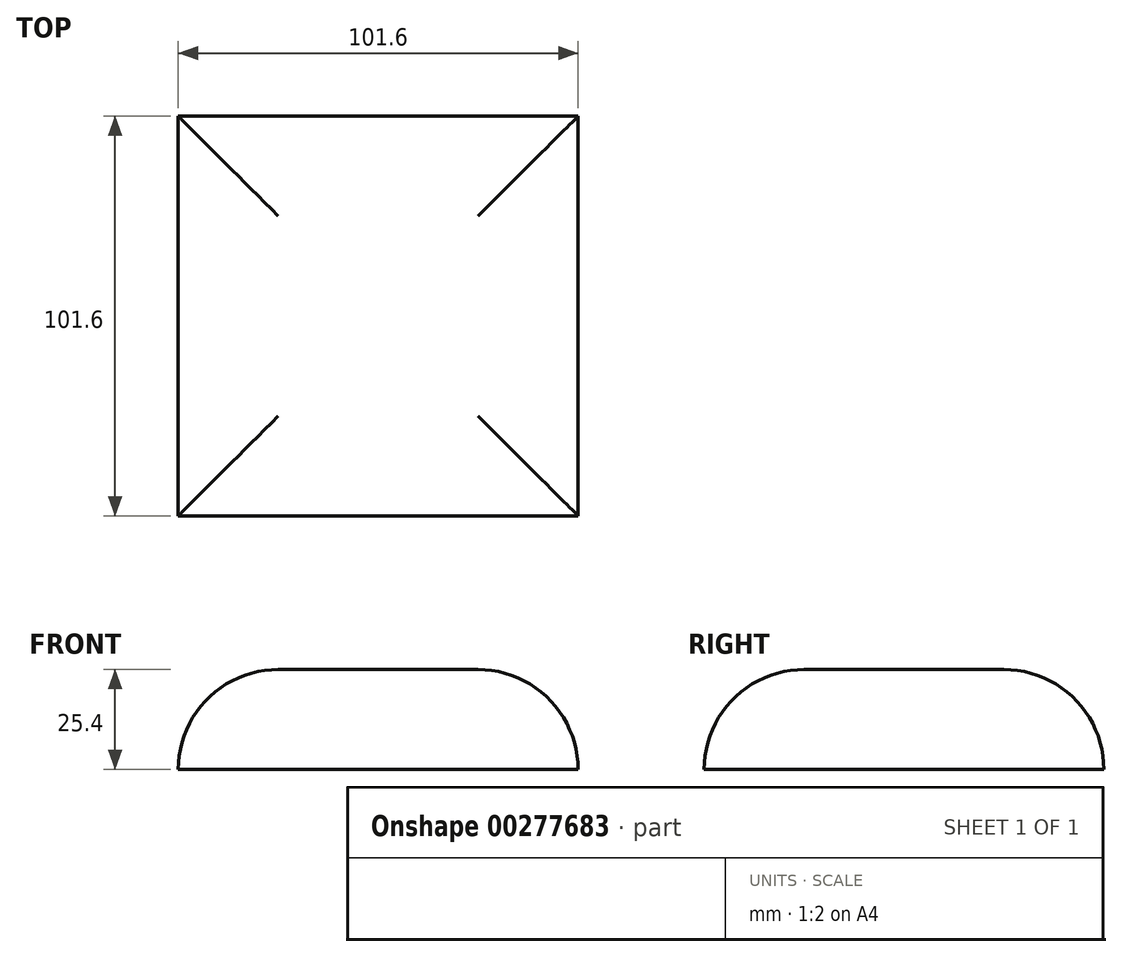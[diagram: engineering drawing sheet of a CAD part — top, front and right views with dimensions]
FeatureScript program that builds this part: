
annotation { "Feature Type Name" : "Feature", "Feature Type Description" : "" }
export const myFeature = defineFeature(function(context is Context, id is Id, definition is map)
    precondition{}
    {
        {
            var Q0;
            Q0=qCreatedBy(makeId("Right.planeOp"),FACE);
            cPlane(context, id + "F0", {"entities" : qUnion([Q0]), "cplaneType" : CPlaneType.OFFSET, "offset" : 127 * mm, "width" : 152.4 * mm, "height" : 152.4 * mm});
        }
        {
            var Q0;
            Q0=qCreatedBy(id+"F0.planeOp",FACE);
            var sketch = newSketch(context, id + "F1", { "sketchPlane" : qUnion([Q0])});
            skEllipse(sketch, "E0", {"center": v(46.36, -7.32) * mm, "majorRadius": 60.94 * mm, "minorRadius": 55.55 * mm, "majorAxis": v(-0.96, -0.3)});
            skSolve(sketch);
        }
        {
            var Q0;
            Q0=qCreatedBy(makeId("Top.planeOp"),FACE);
            cPlane(context, id + "F2", {"entities" : qUnion([Q0]), "cplaneType" : CPlaneType.OFFSET, "offset" : 254 * mm, "width" : 152.4 * mm, "height" : 152.4 * mm});
        }
        {
            var Q0;
            Q0=qCreatedBy(id+"F2.planeOp",FACE);
            var sketch = newSketch(context, id + "F3", { "sketchPlane" : qUnion([Q0])});
            skLineSegment(sketch, "E1.bottom", {"start": v(-33.88, 33.33) * mm, "end": v(16.85, 33.33) * mm});
            skLineSegment(sketch, "E1.top", {"start": v(-33.88, -36.58) * mm, "end": v(16.85, -36.58) * mm});
            skLineSegment(sketch, "E1.left", {"start": v(-33.88, 33.33) * mm, "end": v(-33.88, -36.58) * mm});
            skLineSegment(sketch, "E1.right", {"start": v(16.85, 33.33) * mm, "end": v(16.85, -36.58) * mm});
            skSolve(sketch);
        }
        {
            var Q0;
            Q0=makeQuery(id+"F1.imprint","IMPRINT",FACE,{"disambiguationData":[TD([[makeQuery(id+"F1.imprint","IMPRINT",EDGE,{"derivedFrom":sQuery(id+"F1.wireOp",EDGE,"E0")}),1.0]])]});
            var Q1;
            Q1=makeQuery(id+"F3.imprint","IMPRINT",FACE,{"disambiguationData":[TD([[makeQuery(id+"F3.imprint","IMPRINT",EDGE,{"derivedFrom":sQuery(id+"F3.wireOp",EDGE,"E1.bottom")}),-1.0]])]});
            loft(context, id + "F4", {"sheetProfilesArray" : [{ "sheetProfileEntities" : qUnion([Q0]) }, { "sheetProfileEntities" : qUnion([Q1]) }]});
        }
        {
            var Q0;
            Q0=makeQuery(id+"F4.opLoft","SWEPT_BODY",BODY,{"disambiguationData":[OSD([makeQuery(id+"F1.imprint","IMPRINT",FACE,{"disambiguationData":[TD([[makeQuery(id+"F1.imprint","IMPRINT",EDGE,{"derivedFrom":sQuery(id+"F1.wireOp",EDGE,"E0")}),1.0]])]}),makeQuery(id+"F3.imprint","IMPRINT",FACE,{"disambiguationData":[TD([[makeQuery(id+"F3.imprint","IMPRINT",EDGE,{"derivedFrom":sQuery(id+"F3.wireOp",EDGE,"E1.bottom")}),-1.0]])]})])]});
            deleteBodies(context, id + "F5", {"entities" : qUnion([Q0])});
        }
        {
            var Q0;
            Q0=qCreatedBy(id+"F2.planeOp",FACE);
            var sketch = newSketch(context, id + "F6", { "sketchPlane" : qUnion([Q0])});
            skLineSegment(sketch, "E2.bottom", {"start": v(-51.27, 57.3) * mm, "end": v(50.33, 57.3) * mm});
            skLineSegment(sketch, "E2.top", {"start": v(-51.27, -44.3) * mm, "end": v(50.33, -44.3) * mm});
            skLineSegment(sketch, "E2.left", {"start": v(-51.27, 57.3) * mm, "end": v(-51.27, -44.3) * mm});
            skLineSegment(sketch, "E2.right", {"start": v(50.33, 57.3) * mm, "end": v(50.33, -44.3) * mm});
            skSolve(sketch);
        }
        {
            var Q0;
            Q0 = qSketchRegion(id + "F6", true);
            extrude(context, id + "F7", {"entities" : qUnion([Q0]), "depth" : 25.4 * mm});
        }
        {
            var Q0;
            Q0=makeQuery(id+"F7.opExtrude","CAP_FACE",FACE,{"disambiguationData":[OSD([sQuery(id+"F6.wireOp",EDGE,"E2.bottom"),sQuery(id+"F6.wireOp",EDGE,"E2.top"),sQuery(id+"F6.wireOp",EDGE,"E2.left"),sQuery(id+"F6.wireOp",EDGE,"E2.right")])],"isStart":false});
            fillet(context, id + "F8", {"entities" : qUnion([Q0]), "radius" : 25.4 * mm, "tangentPropagation" : true, "allowEdgeOverflow" : false});
        }
    });
